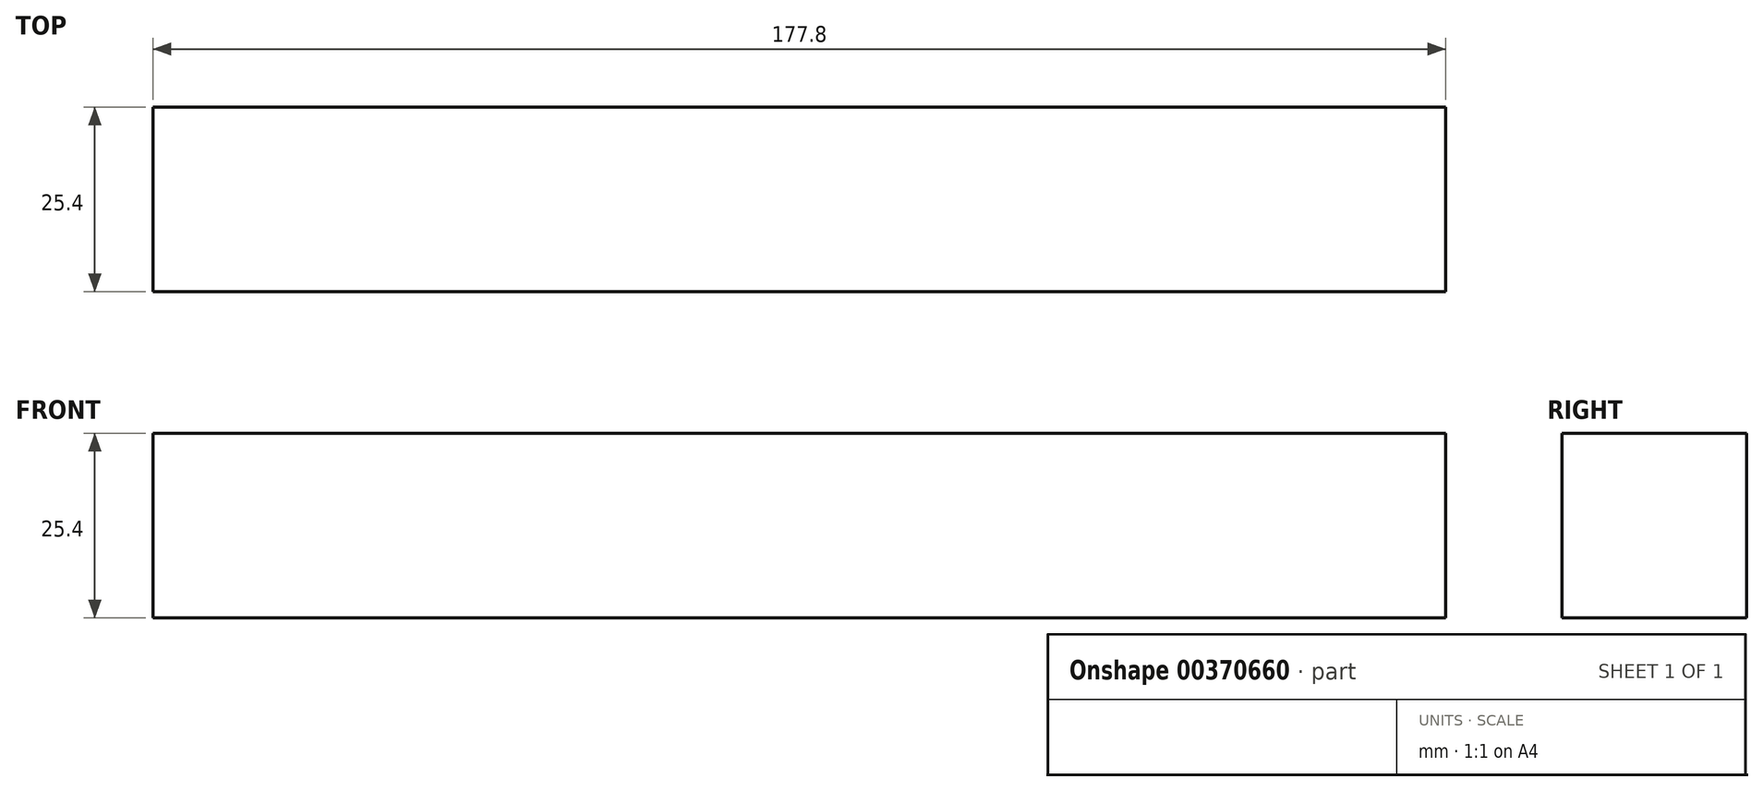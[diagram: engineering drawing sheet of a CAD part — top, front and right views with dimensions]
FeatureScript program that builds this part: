
annotation { "Feature Type Name" : "Feature", "Feature Type Description" : "" }
export const myFeature = defineFeature(function(context is Context, id is Id, definition is map)
    precondition{}
    {
        {
            var Q0;
            Q0=qCreatedBy(makeId("Front.planeOp"),FACE);
            var sketch = newSketch(context, id + "F0", { "sketchPlane" : qUnion([Q0])});
            skLineSegment(sketch, "E0.bottom", {"start": v(0, 0) * mm, "end": v(177.8, 0) * mm});
            skLineSegment(sketch, "E0.top", {"start": v(0, 25.4) * mm, "end": v(177.8, 25.4) * mm});
            skLineSegment(sketch, "E0.left", {"start": v(0, 0) * mm, "end": v(0, 25.4) * mm});
            skLineSegment(sketch, "E0.right", {"start": v(177.8, 0) * mm, "end": v(177.8, 25.4) * mm});
            skSolve(sketch);
        }
        {
            var Q0;
            Q0 = qSketchRegion(id + "FjXXvLYhKXpDFrf_0", true);
            var Q1;
            Q1 = qSketchRegion(id + "F0", true);
            extrude(context, id + "F1", {"entities" : qUnion([Q0, Q1]), "depth" : 25.4 * mm});
        }
    });
